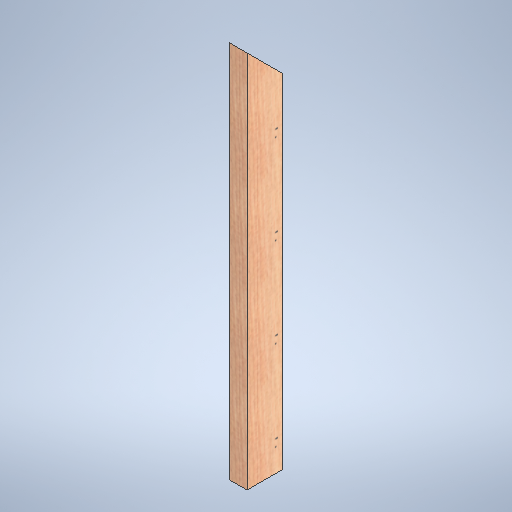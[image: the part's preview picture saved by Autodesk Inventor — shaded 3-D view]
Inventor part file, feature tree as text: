
AUTODESK INVENTOR PART (.ipt)
format: ipt  version: 2025 (Build 290162000, 162)  size: 320,512 bytes
history: native  units: in
note: dims shown in document units (in); Inventor stores cm internally (conversion verified against a paired STEP export)
features: extrude x2, sketch x2
ambient origin geometry x8: Origin, YZ Plane, XZ Plane, XY Plane, X Axis, Y Axis, Z Axis, Center Point
bodies: Solid1 (feature_tree)
feature tree (4):
  extrude  "Extrusion1"  Depth=4.0in
  extrude  "Extrusion2"  TaperAngle=45.0deg  [1 undecoded]
  sketch  "Sketch1"  dims[d0=2.0in d1=4.0in]
  sketch  "Sketch2"  dims[d2=42.34in d3=0.0in d4=45.0deg d5=2.0in d6=0.0in]
note: 1 required parameter value undecoded (feature->parameter linkage not recoverable at this tier; creation-order binding heuristic only, values carry confidence <= 0.55)
